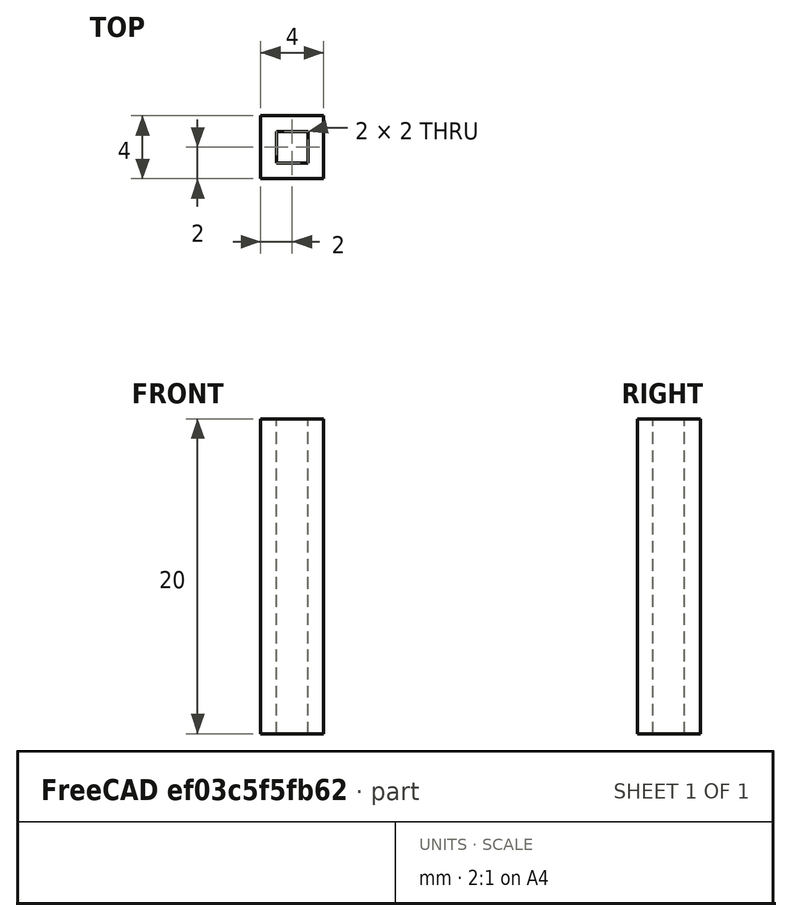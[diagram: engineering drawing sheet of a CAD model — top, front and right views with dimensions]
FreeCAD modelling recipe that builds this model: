
FCSTD DOCUMENT  (FreeCAD 0.18.1R)
Label: shub4R
License: All rights reserved
LicenseURL: http://en.wikipedia.org/wiki/All_rights_reserved
objects: TechDraw::DrawViewDimension×6, TechDraw::DrawProjGroupItem×4, Sketcher::SketchObject×2, PartDesign::Pad×1, PartDesign::Plane×1, PartDesign::Pocket×1, PartDesign::Body×1, TechDraw::DrawSVGTemplate×1, TechDraw::DrawProjGroup×1, TechDraw::DrawPage×1
note: 8 computed .brp shape members not serialized (recipe doc carries the construction recipe); baked Part::Feature solids carry a one-line shape summary decoded from their .brp

FEATURE [Sketcher::SketchObject] Sketch
  MapMode = 5
  Support = -> [XY_Plane]
  sketch-geometry (4):
    g0: LineSegment StartX=0 StartY=4 StartZ=0 EndX=4 EndY=4 EndZ=0
    g1: LineSegment StartX=4 StartY=4 StartZ=0 EndX=4 EndY=0 EndZ=0
    g2: LineSegment StartX=4 StartY=0 StartZ=0 EndX=0 EndY=0 EndZ=0
    g3: LineSegment StartX=0 StartY=0 StartZ=0 EndX=0 EndY=4 EndZ=0
  constraints (11):
    c: Coincident(g0,g1)
    c: Coincident(g1,g2)
    c: Coincident(g2,g3)
    c: Coincident(g3,g0)
    c: Horizontal(g0)
    c: Horizontal(g2)
    c: Vertical(g1)
    c: Vertical(g3)
    c: DistanceX(g0,g0) = 4
    c: DistanceY(g1,g1) = 4
    c: Coincident(g2,g-1)
FEATURE [PartDesign::Pad] Pad
  Length = 20
  Length2 = 100
  Profile = -> Sketch
  Type = 0
FEATURE [PartDesign::Plane] DatumPlane
  Length = 24
  MapMode = 5
  Placement = pos=(0,0,0) rot=(1,0,0;3.14159rad)
  ResizeMode = 0
  Support = -> [Pad]
  Width = 24
FEATURE [Sketcher::SketchObject] Sketch001
  ExternalGeometry = -> [Pad]
  MapMode = 5
  Placement = pos=(0,0,0) rot=(1,0,0;3.14159rad)
  Support = -> [DatumPlane]
  sketch-geometry (4):
    g0: LineSegment StartX=1 StartY=-3 StartZ=0 EndX=3 EndY=-3 EndZ=0
    g1: LineSegment StartX=3 StartY=-3 StartZ=0 EndX=3 EndY=-1 EndZ=0
    g2: LineSegment StartX=3 StartY=-1 StartZ=0 EndX=1 EndY=-1 EndZ=0
    g3: LineSegment StartX=1 StartY=-1 StartZ=0 EndX=1 EndY=-3 EndZ=0
  constraints (12):
    c: Coincident(g0,g1)
    c: Coincident(g1,g2)
    c: Coincident(g2,g3)
    c: Coincident(g3,g0)
    c: Horizontal(g0)
    c: Horizontal(g2)
    c: Vertical(g1)
    c: Vertical(g3)
    c: DistanceX(g2,g2) = 2
    c: DistanceY(g3,g3) = 2
    c: Distance(g0,g-4) = 1
    c: Distance(g0,g-3) = 1
FEATURE [PartDesign::Pocket] Pocket
  BaseFeature = -> Pad
  Length = 20
  Length2 = 100
  Profile = -> Sketch001
  Type = 0
FEATURE [PartDesign::Body] Body
  Group = -> [Sketch,Pad,DatumPlane,Sketch001,Pocket]
  Origin = -> Origin
  Tip = -> Pocket
FEATURE [TechDraw::DrawSVGTemplate] Template
  EditableTexts = Designed_by_Name=Designed by Name; Drawing_number=Drawing number; FC-Date=Date; FC-SC=Scale; FC-SH=Sheet; FC-Title=Title; Subtitle=Subtitle; Weight=Weight
  Height = 210
  Orientation = 1
  Width = 297
FEATURE [TechDraw::DrawProjGroupItem] ProjItem  label="Front"
  CoarseView = false
  Direction = (0,-1,0)
  Focus = 100
  HardHidden = false
  IsoCount = 0
  IsoHidden = false
  IsoVisible = false
  LockPosition = true
  Perspective = false
  Rotation = 0
  RotationVector = (1,0,0)
  Scale = 3
  ScaleType = 2
  SeamHidden = false
  SeamVisible = false
  SmoothHidden = false
  SmoothVisible = false
  Source = -> [Pocket]
  Type = 0
  X = 0
  Y = 0
FEATURE [TechDraw::DrawProjGroupItem] ProjItem001  label="FrontTopLeft"
  CoarseView = false
  Direction = (-1,-1,1)
  Focus = 100
  HardHidden = false
  IsoCount = 0
  IsoHidden = false
  IsoVisible = false
  LockPosition = false
  Perspective = false
  Rotation = 0
  RotationVector = (1,-1,0)
  Scale = 3
  ScaleType = 2
  SeamHidden = false
  SeamVisible = false
  SmoothHidden = false
  SmoothVisible = false
  Source = -> [Pocket]
  Type = 6
  X = 75
  Y = -84.1415
FEATURE [TechDraw::DrawProjGroupItem] ProjItem002  label="Top"
  CoarseView = false
  Direction = (0,0,1)
  Focus = 100
  HardHidden = false
  IsoCount = 0
  IsoHidden = false
  IsoVisible = false
  LockPosition = false
  Perspective = false
  Rotation = 0
  RotationVector = (1,0,0)
  Scale = 3
  ScaleType = 2
  SeamHidden = false
  SeamVisible = false
  SmoothHidden = false
  SmoothVisible = false
  Source = -> [Pocket]
  Type = 4
  X = 0
  Y = -75
FEATURE [TechDraw::DrawProjGroupItem] ProjItem003  label="Left"
  CoarseView = false
  Direction = (-1,-1e-16,0)
  Focus = 100
  HardHidden = false
  IsoCount = 0
  IsoHidden = false
  IsoVisible = false
  LockPosition = false
  Perspective = false
  Rotation = 0
  RotationVector = (1e-16,-1,0)
  Scale = 3
  ScaleType = 2
  SeamHidden = false
  SeamVisible = false
  SmoothHidden = false
  SmoothVisible = false
  Source = -> [Pocket]
  Type = 1
  X = 75
  Y = 0
FEATURE [TechDraw::DrawProjGroup] ProjGroup
  Anchor = -> ProjItem
  AutoDistribute = true
  LockPosition = false
  ProjectionType = 1
  Rotation = 0
  Scale = 3
  ScaleType = 0
  Source = -> [Pocket]
  Views = -> [ProjItem,ProjItem001,ProjItem002,ProjItem003]
  X = 44.6189
  Y = 167.329
  spacingX = 15
  spacingY = 15
FEATURE [TechDraw::DrawViewDimension] Dimension
  Arbitrary = false
  FormatSpec = %.2f
  LockPosition = false
  MeasureType = 1
  OverTolerance = 0
  References2D = -> [ProjItem]
  Rotation = 0
  Scale = 3
  ScaleType = 0
  Type = 2
  UnderTolerance = 0
  X = 16.3881
  Y = -3.3242
FEATURE [TechDraw::DrawViewDimension] Dimension001
  Arbitrary = false
  FormatSpec = %.2f
  LockPosition = false
  MeasureType = 1
  OverTolerance = 0
  References2D = -> [ProjItem]
  Rotation = 0
  Scale = 3
  ScaleType = 0
  Type = 1
  UnderTolerance = 0
  X = 2.49315
  Y = -42.0502
FEATURE [TechDraw::DrawViewDimension] Dimension002
  Arbitrary = false
  FormatSpec = %.2f
  LockPosition = false
  MeasureType = 1
  OverTolerance = 0
  References2D = -> [ProjItem003]
  Rotation = 0
  Scale = 3
  ScaleType = 0
  Type = 2
  UnderTolerance = 0
  X = 18.8813
  Y = -5.81734
FEATURE [TechDraw::DrawViewDimension] Dimension003
  Arbitrary = false
  FormatSpec = %.2f
  LockPosition = false
  MeasureType = 1
  OverTolerance = 0
  References2D = -> [ProjItem003]
  Rotation = 0
  Scale = 3
  ScaleType = 0
  Type = 1
  UnderTolerance = 0
  X = 2.90867
  Y = -42.0502
FEATURE [TechDraw::DrawViewDimension] Dimension004
  Arbitrary = false
  FormatSpec = %.2f
  LockPosition = false
  MeasureType = 1
  OverTolerance = 0
  References2D = -> [ProjItem002]
  Rotation = 0
  Scale = 3
  ScaleType = 0
  Type = 1
  UnderTolerance = 0
  X = 22.0228
  Y = -40.073
FEATURE [TechDraw::DrawViewDimension] Dimension005
  Arbitrary = false
  FormatSpec = %.2f
  LockPosition = false
  MeasureType = 1
  OverTolerance = 0
  References2D = -> [ProjItem002]
  Rotation = 0
  Scale = 3
  ScaleType = 0
  Type = 2
  UnderTolerance = 0
  X = 23.7762
  Y = 12.4657
FEATURE [TechDraw::DrawPage] Page
  KeepUpdated = true
  ProjectionType = 0
  Scale = 3
  Template = -> Template
  Views = -> [ProjGroup,Dimension,Dimension001,Dimension002,Dimension003,Dimension004,Dimension005]
